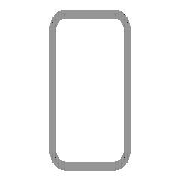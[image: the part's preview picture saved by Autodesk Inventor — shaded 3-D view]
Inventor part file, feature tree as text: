
AUTODESK INVENTOR PART (.ipt)
format: ipt  version: 2025.1 (Build 291241020, 241B)  size: 143,360 bytes
history: native  units: mm (DEFAULTED — no unit token found)
features: other x4, plane x2, split x1, sketch x1
ambient origin geometry x8: Origin, YZ Plane, XZ Plane, XY Plane, X Axis, Y Axis, Z Axis, Center Point
bodies: Solid1 (feature_tree), Body (feature_tree)
feature tree (8):
  parser-record x1  (decoder bookkeeping rows leaked as tree rows — omitted from the tree; the rows remain in map.json)
  other  "Driven Length"
  other  "Start Plane"
  other  "End Plane"
  plane  "Work Plane4"
  split  "Split1"
  sketch  "Sketch3"  dims[d3=279.948996mm d4=0.0mm d7=6.0mm d9=40.0mm d11=80.0mm d12=3.0mm d13=65.051004mm d14=345.0mm d15=20.0mm d16=40.0mm d17=90.0deg d18=279.948996mm]
  plane  "Work Plane3"
